# Revit family: Krowne_HS-3819_Sink
name_source: partatom
category: Plumbing Fixtures
revit_build: Autodesk Revit 2018 (Build: 20190510_1515(x64)
units: mm (PartAtom-declared; Revit-internal decimal feet)

## family parameters
Always vertical = Yes
Cut with Voids When Loaded = No
OmniClass Number = 23.40.40.00
OmniClass Title = Food Service Equipment and Furnishings
Part Type = Normal
Room Calculation Point = No
Round Connector Dimension = Use Diameter
Shared = No
Work Plane-Based = No

## types (1)
- HS-3819
    Assembly Code = E1090300
    Cold Water Connection Height = 0"
    Cold Water Flow = 1 GPM
    Cold Water Maximum Pressure = 0.00 psi
    Cold Water Minimum Pressure = 0.00 psi
    Cold Water Size = 1"
    Cold Water Temperature Recommended = -460 °F
    Depth = 18"
    Description = 36" X 18" Three Compartment Drop-In Sink
    Direct Waste Size = 2"
    Foodservice Equipment Identifier = Yes
    Height = 3 3/8"
    Hot Water Connection Height = 0"
    Hot Water Consumption = 0 GPM
    Hot Water Flow = 1 GPM
    Hot Water Maximum Pressure = 0.00 psi
    Hot Water Minimum Pressure = 0.00 psi
    Hot Water Size = 1"
    Hot Water Temperature = -460 °F
    Indirect Waste Flow = 0 GPM
    Indirect Waste Size = 4"
    Manufacturer = Krowne Metal
    Model = HS-3819
    URL = https://krowne.com
    Weight in Pounds = 45
    Width = 36"

## geometry (parser evidence)
native form markers: Sweep x3
no freeform markers — native parametric forms only
